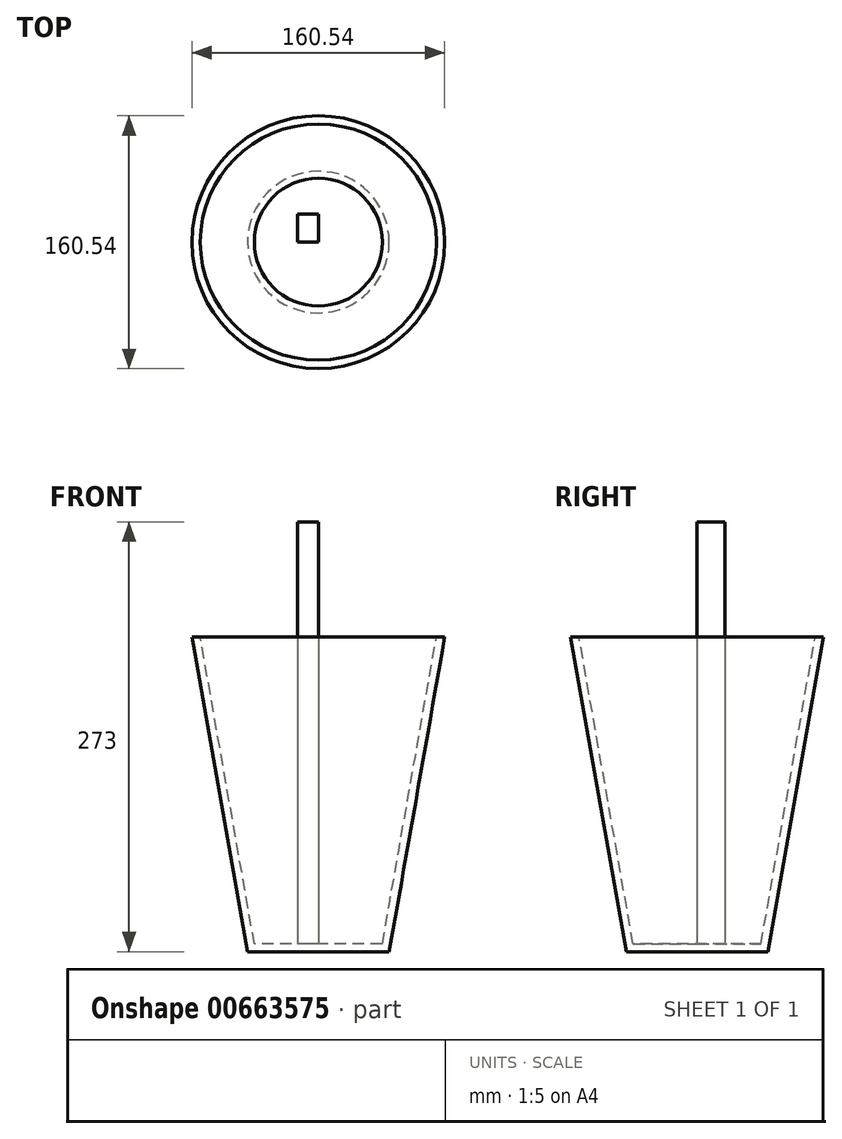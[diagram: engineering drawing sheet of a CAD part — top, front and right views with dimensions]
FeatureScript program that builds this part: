
annotation { "Feature Type Name" : "Feature", "Feature Type Description" : "" }
export const myFeature = defineFeature(function(context is Context, id is Id, definition is map)
    precondition{}
    {
        {
            var Q0;
            Q0=qCreatedBy(makeId("Top.planeOp"),FACE);
            var sketch = newSketch(context, id + "F0", { "sketchPlane" : qUnion([Q0])});
            skCircle(sketch, "E0", {"center": v(0, 0) * mm, "radius": 45 * mm});
            skSolve(sketch);
        }
        {
            var Q0;
            Q0 = qSketchRegion(id + "F0", true);
            extrude(context, id + "F1", {"entities" : qUnion([Q0]), "depth" : 200 * mm, "offsetDistance" : 25 * mm, "hasDraft" : true, "draftAngle" : 10 * degree});
        }
        {
            var Q0;
            Q0=makeQuery(id+"F1.opExtrude","CAP_FACE",FACE,{"disambiguationData":[OSD([sQuery(id+"F0.wireOp",EDGE,"E0")])],"isStart":false});
            var sketch = newSketch(context, id + "F2", { "sketchPlane" : qUnion([Q0])});
            skCircle(sketch, "E1", {"center": v(0, 0) * mm, "radius": 75 * mm});
            skSolve(sketch);
        }
        {
            var Q0;
            Q0=makeQuery(id+"F2.imprint","IMPRINT",FACE,{"disambiguationData":[TD([[makeQuery(id+"F2.imprint","IMPRINT",EDGE,{"derivedFrom":sQuery(id+"F2.wireOp",EDGE,"E1")}),1.0]])]});
            extrude(context, id + "F3", {"entities" : qUnion([Q0]), "operationType" : NewBodyOperationType.REMOVE, "oppositeDirection" : true, "depth" : 195 * mm, "offsetDistance" : 25 * mm, "hasDraft" : true, "draftAngle" : 10 * degree, "draftPullDirection" : true});
        }
        {
            var Q0;
            Q0=qCreatedBy(makeId("Top.planeOp"),FACE);
            cPlane(context, id + "F4", {"entities" : qUnion([Q0]), "cplaneType" : CPlaneType.OFFSET, "offset" : 5 * mm, "width" : 150 * mm, "height" : 150 * mm});
        }
        {
            var Q0;
            Q0=qCreatedBy(id+"F4.planeOp",FACE);
            var sketch = newSketch(context, id + "F5", { "sketchPlane" : qUnion([Q0])});
            skLineSegment(sketch, "E2.bottom", {"start": v(0, 0) * mm, "end": v(-13.15, 0) * mm});
            skLineSegment(sketch, "E2.top", {"start": v(0, 17.7) * mm, "end": v(-13.15, 17.7) * mm});
            skLineSegment(sketch, "E2.left", {"start": v(0, 0) * mm, "end": v(0, 17.7) * mm});
            skLineSegment(sketch, "E2.right", {"start": v(-13.15, 0) * mm, "end": v(-13.15, 17.7) * mm});
            skSolve(sketch);
        }
        {
            var Q0;
            Q0 = qSketchRegion(id + "F5", true);
            extrude(context, id + "F6", {"entities" : qUnion([Q0]), "operationType" : NewBodyOperationType.ADD, "depth" : 268 * mm, "offsetDistance" : 25 * mm});
        }
    });
